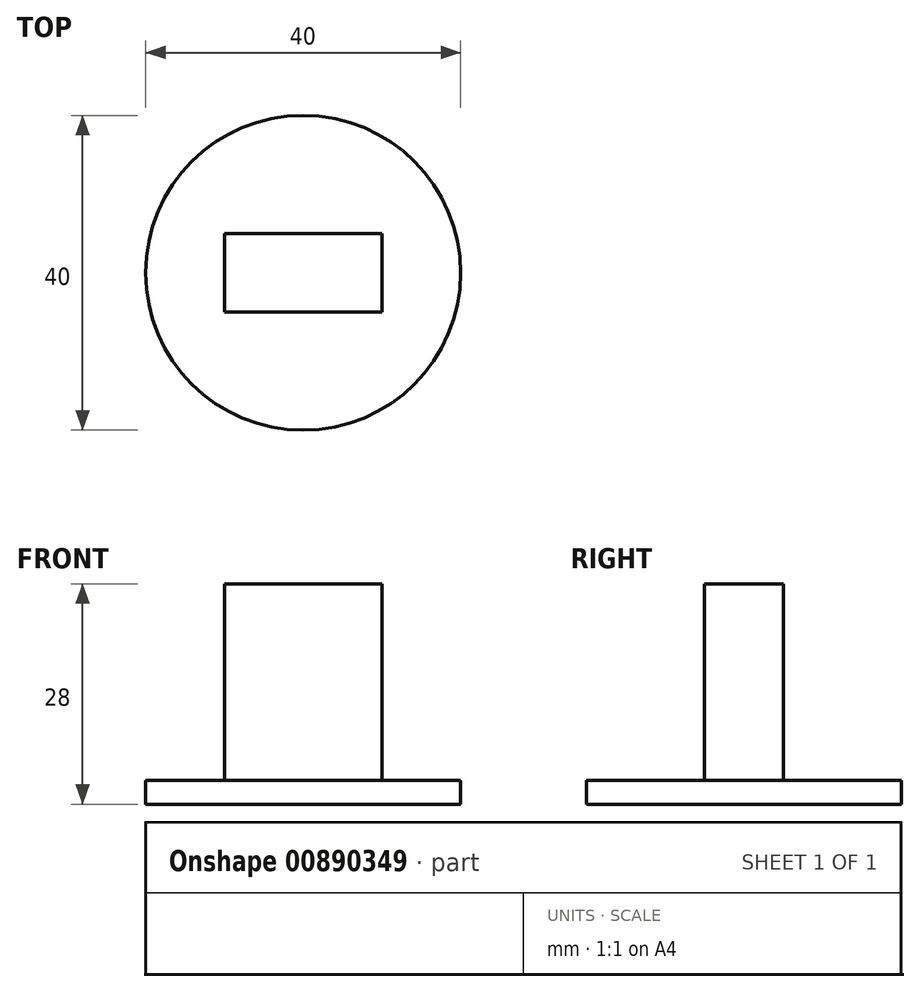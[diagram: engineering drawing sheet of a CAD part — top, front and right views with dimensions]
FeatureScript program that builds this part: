
annotation { "Feature Type Name" : "Feature", "Feature Type Description" : "" }
export const myFeature = defineFeature(function(context is Context, id is Id, definition is map)
    precondition{}
    {
        {
            var Q0;
            Q0=qCreatedBy(makeId("Top.planeOp"),FACE);
            var sketch = newSketch(context, id + "F0", { "sketchPlane" : qUnion([Q0])});
            skCircle(sketch, "E0", {"center": v(0, 0) * mm, "radius": 20 * mm});
            skSolve(sketch);
        }
        {
            var Q0;
            Q0=makeQuery(id+"F0.imprint","IMPRINT",FACE,{"disambiguationData":[TD([[makeQuery(id+"F0.imprint","IMPRINT",EDGE,{"derivedFrom":sQuery(id+"F0.wireOp",EDGE,"E0")}),1.0]])]});
            extrude(context, id + "F1", {"entities" : qUnion([Q0]), "depth" : 3 * mm, "offsetDistance" : 25 * mm});
        }
        {
            var Q0;
            Q0=makeQuery(id+"F1.opExtrude","CAP_FACE",FACE,{"disambiguationData":[OSD([sQuery(id+"F0.wireOp",EDGE,"E0")])],"isStart":false});
            var sketch = newSketch(context, id + "F2", { "sketchPlane" : qUnion([Q0])});
            skLineSegment(sketch, "E1.bottom", {"start": v(-10, 5) * mm, "end": v(10, 5) * mm});
            skLineSegment(sketch, "E1.top", {"start": v(-10, -5) * mm, "end": v(10, -5) * mm});
            skLineSegment(sketch, "E1.left", {"start": v(-10, 5) * mm, "end": v(-10, -5) * mm});
            skLineSegment(sketch, "E1.right", {"start": v(10, 5) * mm, "end": v(10, -5) * mm});
            skSolve(sketch);
        }
        {
            var Q0;
            Q0=makeQuery(id+"F2.imprint","IMPRINT",FACE,{"disambiguationData":[TD([[makeQuery(id+"F2.imprint","IMPRINT",EDGE,{"derivedFrom":sQuery(id+"F2.wireOp",EDGE,"E1.bottom")}),-1.0]])]});
            extrude(context, id + "F3", {"entities" : qUnion([Q0]), "depth" : 25 * mm, "offsetDistance" : 25 * mm});
        }
    });
